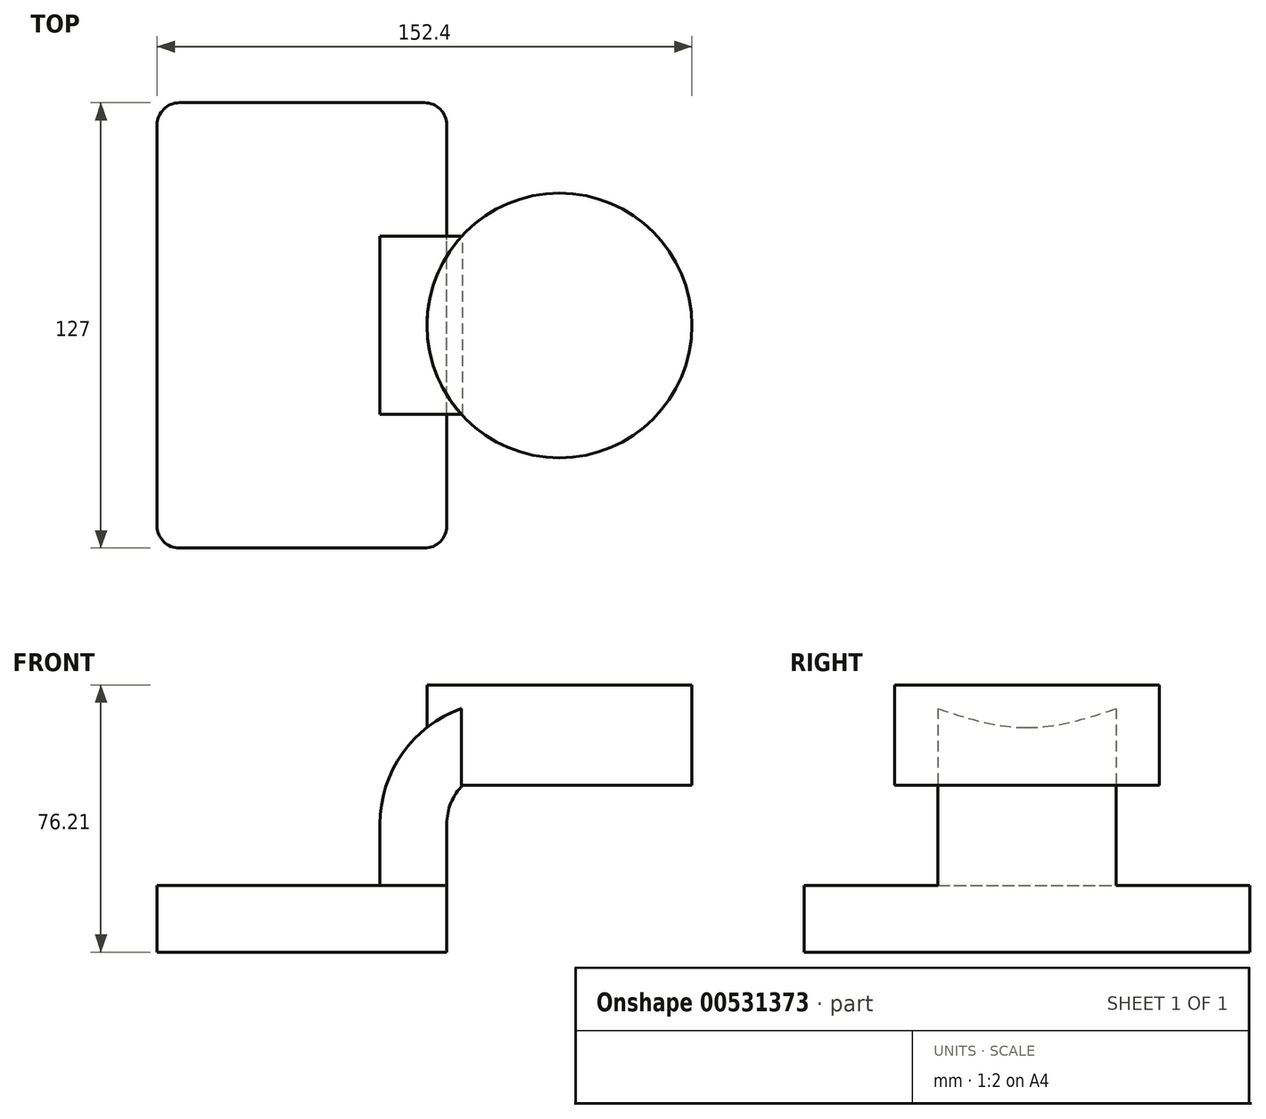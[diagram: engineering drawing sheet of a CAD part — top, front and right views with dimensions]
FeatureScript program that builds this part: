
annotation { "Feature Type Name" : "Feature", "Feature Type Description" : "" }
export const myFeature = defineFeature(function(context is Context, id is Id, definition is map)
    precondition{}
    {
        {
            var Q0;
            Q0=qCreatedBy(makeId("Front.planeOp"),FACE);
            var sketch = newSketch(context, id + "F0", { "sketchPlane" : qUnion([Q0])});
            skLineSegment(sketch, "E0.bottom", {"start": v(-41.28, -9.52) * mm, "end": v(41.28, -9.53) * mm});
            skLineSegment(sketch, "E0.top", {"start": v(-41.28, 9.52) * mm, "end": v(41.28, 9.52) * mm});
            skLineSegment(sketch, "E0.left", {"start": v(-41.28, -9.52) * mm, "end": v(-41.28, 9.53) * mm});
            skLineSegment(sketch, "E0.right", {"start": v(41.28, -9.53) * mm, "end": v(41.28, 9.52) * mm});
            skPoint(sketch, "E0.middle", {"position": v(0, 0) * mm});
            skLineSegment(sketch, "E1.bottom", {"start": v(60.32, 38.1) * mm, "end": v(111.12, 38.1) * mm});
            skLineSegment(sketch, "E1.top", {"start": v(60.32, 66.68) * mm, "end": v(111.12, 66.68) * mm});
            skLineSegment(sketch, "E1.left", {"start": v(60.32, 38.1) * mm, "end": v(60.32, 66.68) * mm});
            skLineSegment(sketch, "E1.right", {"start": v(111.12, 38.1) * mm, "end": v(111.12, 66.68) * mm});
            skPoint(sketch, "E1.middle", {"position": v(85.72, 52.39) * mm});
            skLineSegment(sketch, "E2", {"start": v(41.28, 9.52) * mm, "end": v(41.28, 27) * mm});
            skArc(sketch, "E3", {"start": v(41.28, 27) * mm, "mid": v(45.92, 38.23) * mm, "end": v(57.15, 42.88) * mm});
            skLineSegment(sketch, "E4", {"start": v(57.15, 42.88) * mm, "end": v(73.38, 42.88) * mm});
            skLineSegment(sketch, "E5.0", {"start": v(57.15, 61.93) * mm, "end": v(73.38, 61.93) * mm});
            skArc(sketch, "E5.1", {"start": v(22.23, 27) * mm, "mid": v(32.45, 51.7) * mm, "end": v(57.15, 61.93) * mm});
            skLineSegment(sketch, "E5.2", {"start": v(22.23, 9.52) * mm, "end": v(22.23, 27) * mm});
            skLineSegment(sketch, "E6", {"start": v(73.38, 38.1) * mm, "end": v(73.38, 42.88) * mm});
            skLineSegment(sketch, "E7", {"start": v(73.38, 42.88) * mm, "end": v(73.38, 61.93) * mm});
            skLineSegment(sketch, "E8", {"start": v(73.38, 61.93) * mm, "end": v(73.38, 66.68) * mm});
            skFitSpline(sketch, "E9", {"points": [v(-41.28, 9.53) * mm, v(57.15, 61.93) * mm], "startDerivative": vector(44.12, 75.55) * mm, "endDerivative": vector(78.84, -42.75) * mm});
            skSolve(sketch);
        }
        {
            var Q0;
            Q0=makeQuery(id+"F0.imprint","IMPRINT",FACE,{"disambiguationData":[TD([[makeQuery(id+"F0.imprint","IMPRINT",EDGE,{"derivedFrom":sQuery(id+"F0.wireOp",EDGE,"E0.bottom")}),1.0]])]});
            extrude(context, id + "F1", {"entities" : qUnion([Q0]), "endBound" : BoundingType.SYMMETRIC, "depth" : 127 * mm, "offsetDistance" : 25.4 * mm});
        }
        {
            var Q0;
            {var subQ1=sQuery(id+"F0.wireOp",EDGE,"E2");Q0=makeQuery(id+"F0.imprint","IMPRINT",FACE,{"disambiguationData":[TD([[makeQuery(id+"F0.imprint","IMPRINT",EDGE,{"derivedFrom":subQ1}),1.0]])]});}
            var Q1;
            {var subQ5=sQuery(id+"F0.wireOp",EDGE,"E7");Q1=makeQuery(id+"F0.imprint","IMPRINT",FACE,{"disambiguationData":[TD([[makeQuery(id+"F0.imprint","IMPRINT",EDGE,{"derivedFrom":subQ5}),1.0]])]});}
            extrude(context, id + "F2", {"entities" : qUnion([Q0, Q1]), "operationType" : NewBodyOperationType.ADD, "endBound" : BoundingType.SYMMETRIC, "depth" : 50.8 * mm, "offsetDistance" : 25.4 * mm});
        }
        {
            var Q0;
            Q0=makeQuery(id+"F0.imprint","IMPRINT",FACE,{"disambiguationData":[TD([[makeQuery(id+"F0.imprint","IMPRINT",EDGE,{"derivedFrom":sQuery(id+"F0.wireOp",EDGE,"E5.1")}),1.0]])]});
            extrude(context, id + "F3", {"entities" : qUnion([Q0]), "operationType" : NewBodyOperationType.ADD, "endBound" : BoundingType.SYMMETRIC, "depth" : 15.88 * mm, "offsetDistance" : 25.4 * mm});
        }
        {
            var Q0;
            {var subQ0=sQuery(id+"F0.wireOp",EDGE,"E1.right");Q0=makeQuery(id+"F0.imprint","IMPRINT",FACE,{"disambiguationData":[TD([[makeQuery(id+"F0.imprint","IMPRINT",EDGE,{"derivedFrom":subQ0}),1.0]])]});}
            var Q1;
            Q1=sQuery(id+"F0.wireOp",EDGE,"E7");
            revolve(context, id + "F4", {"operationType" : NewBodyOperationType.ADD, "entities" : qUnion([Q0]), "axis" : qUnion([Q1]), "revolveType" : RevolveType.FULL});
        }
        {
            var Q0;
            Q0=makeQuery(id+"F1.opExtrude","CAP_EDGE",EDGE,{"disambiguationData":[OSD([sQuery(id+"F0.wireOp",EDGE,"E0.right")])],"isStart":false});
            var Q1;
            Q1=makeQuery(id+"F1.opExtrude","CAP_EDGE",EDGE,{"disambiguationData":[OSD([sQuery(id+"F0.wireOp",EDGE,"E0.left")])],"isStart":false});
            var Q2;
            Q2=makeQuery(id+"F1.opExtrude","CAP_EDGE",EDGE,{"disambiguationData":[OSD([sQuery(id+"F0.wireOp",EDGE,"E0.right")])],"isStart":true});
            var Q3;
            Q3=makeQuery(id+"F1.opExtrude","CAP_EDGE",EDGE,{"disambiguationData":[OSD([sQuery(id+"F0.wireOp",EDGE,"E0.left")])],"isStart":true});
            fillet(context, id + "F5", {"entities" : qUnion([Q0, Q1, Q2, Q3]), "radius" : 6.35 * mm, "tangentPropagation" : true, "allowEdgeOverflow" : false});
        }
    });
